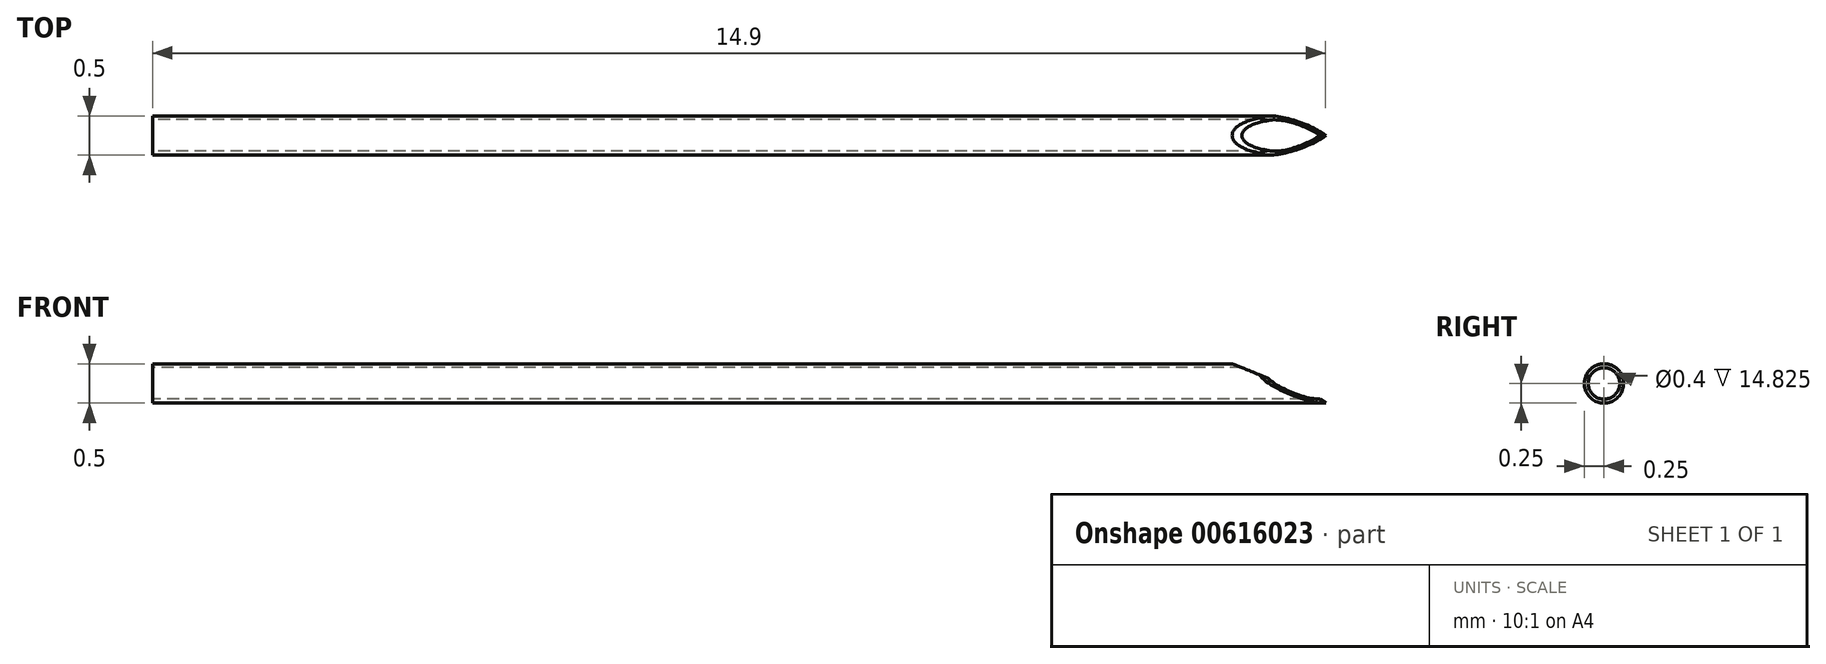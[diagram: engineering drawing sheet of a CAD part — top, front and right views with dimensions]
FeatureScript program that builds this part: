
annotation { "Feature Type Name" : "Feature", "Feature Type Description" : "" }
export const myFeature = defineFeature(function(context is Context, id is Id, definition is map)
    precondition{}
    {
        {
            var Q0;
            Q0=qCreatedBy(makeId("Front.planeOp"),FACE);
            var sketch = newSketch(context, id + "F0", { "sketchPlane" : qUnion([Q0])});
            skLineSegment(sketch, "E0", {"start": v(-2, 0) * mm, "end": v(2.09, 0) * mm, "construction": true});
            skLineSegment(sketch, "E1", {"start": v(-1.43, 0.25) * mm, "end": v(14.57, 0.25) * mm});
            skLineSegment(sketch, "E2", {"start": v(14.57, 0.25) * mm, "end": v(14.57, 0.2) * mm});
            skLineSegment(sketch, "E3", {"start": v(-1.43, 0.2) * mm, "end": v(-1.43, 0.25) * mm});
            skLineSegment(sketch, "E4", {"start": v(14.57, 0.2) * mm, "end": v(-1.43, 0.2) * mm});
            skPoint(sketch, "E5.orphan", {"position": v(-1.43, 0) * mm});
            skPoint(sketch, "E6.orphan", {"position": v(14.57, 0) * mm});
            skSolve(sketch);
        }
        {
            var Q0;
            Q0=qSketchRegion(id+"F0",true);
            var Q1;
            Q1=sQuery(id+"F0.wireOp",EDGE,"E0");
            revolve(context, id + "F1", {"entities" : qUnion([Q0]), "axis" : qUnion([Q1]), "revolveType" : RevolveType.FULL});
        }
        {
            var Q0;
            Q0=qCreatedBy(makeId("Front.planeOp"),FACE);
            var sketch = newSketch(context, id + "F2", { "sketchPlane" : qUnion([Q0])});
            skLineSegment(sketch, "E7", {"start": v(9.86, 1.23) * mm, "end": v(14.99, -0.84) * mm});
            skLineSegment(sketch, "E8", {"start": v(14.99, -0.84) * mm, "end": v(14.99, 1.23) * mm});
            skLineSegment(sketch, "E9", {"start": v(14.99, 1.23) * mm, "end": v(9.86, 1.23) * mm});
            skSolve(sketch);
        }
        {
            var Q0;
            Q0=qSketchRegion(id+"F2",true);
            extrude(context, id + "F3", {"entities" : qUnion([Q0]), "operationType" : NewBodyOperationType.REMOVE, "oppositeDirection" : true, "depth" : 25 * mm, "offsetDistance" : 25 * mm, "symmetric" : true});
        }
        {
            var Q0;
            Q0=qCreatedBy(makeId("Front.planeOp"),FACE);
            var sketch = newSketch(context, id + "F4", { "sketchPlane" : qUnion([Q0])});
            skLineSegment(sketch, "E10", {"start": v(11.43, 1.13) * mm, "end": v(13.7, -0.4) * mm});
            skLineSegment(sketch, "E11", {"start": v(13.7, -0.4) * mm, "end": v(13.7, 1.13) * mm});
            skLineSegment(sketch, "E12", {"start": v(13.7, 1.13) * mm, "end": v(11.43, 1.13) * mm});
            skSolve(sketch);
        }
        {
            var Q0;
            Q0=qSketchRegion(id+"F4",true);
            extrude(context, id + "F5", {"entities" : qUnion([Q0]), "operationType" : NewBodyOperationType.REMOVE, "flatOperationType" : FlatOperationType.REMOVE, "oppositeDirection" : true, "depth" : 5 * mm, "offsetDistance" : 25 * mm, "hasDraft" : true, "draftAngle" : 38 * degree, "domain" : OperationDomain.MODEL, "symmetric" : true});
        }
    });
